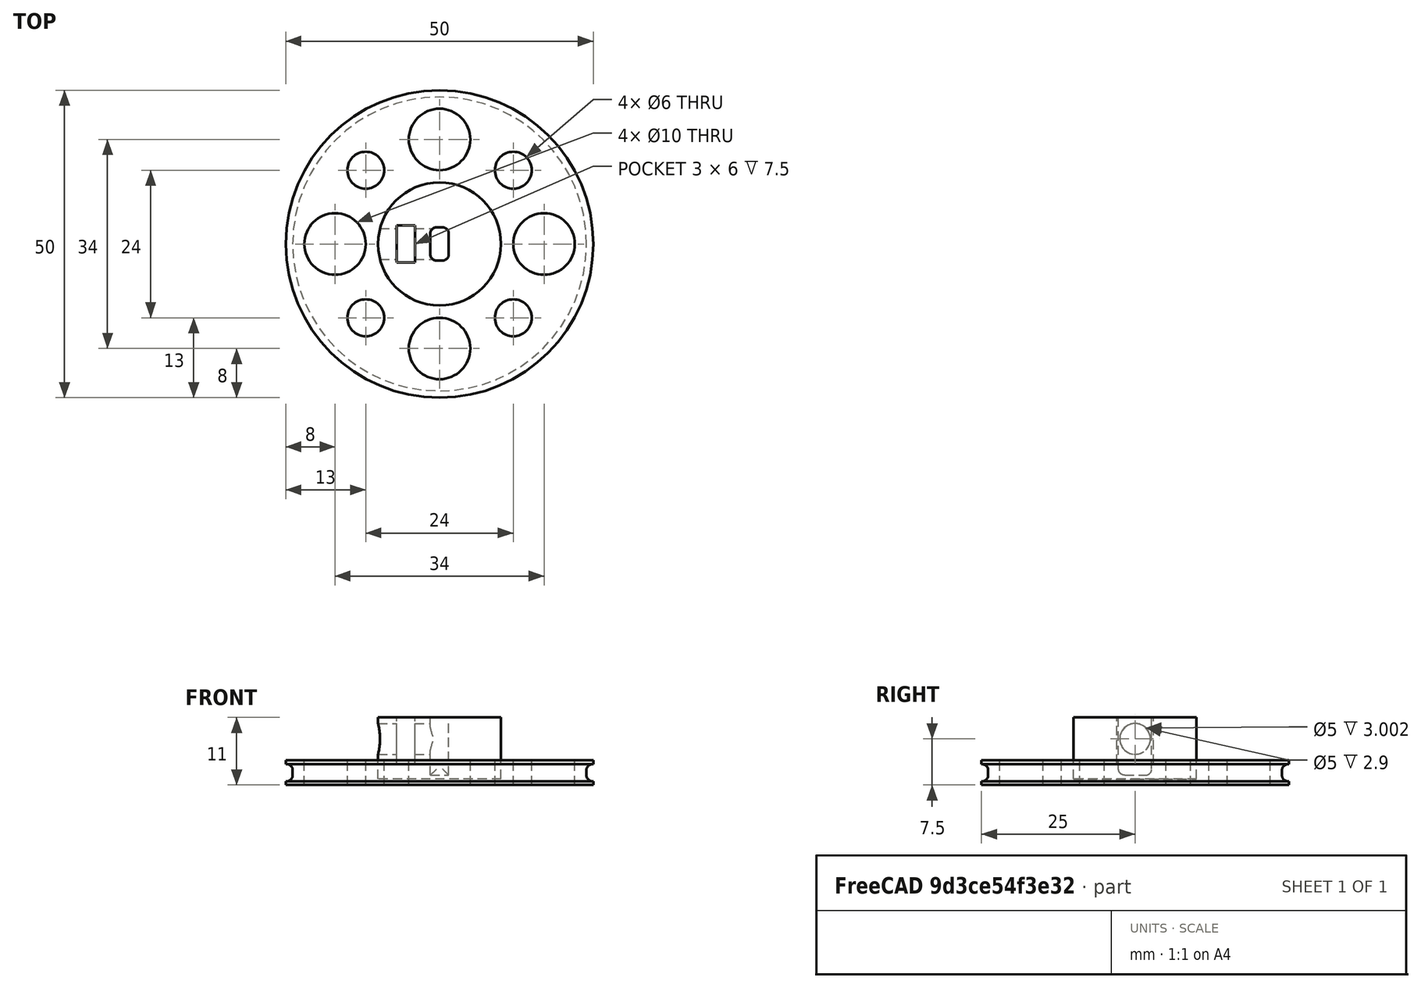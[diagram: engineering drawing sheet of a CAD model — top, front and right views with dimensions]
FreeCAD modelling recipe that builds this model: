
FCSTD DOCUMENT  (FreeCAD 0.18.4R)
Label: ruedas
License: All rights reserved
LicenseURL: http://en.wikipedia.org/wiki/All_rights_reserved
objects: Part::Cylinder×13, Part::Cut×13, Part::Fillet×2, Part::Box×2
note: 30 computed .brp shape members not serialized (recipe doc carries the construction recipe); baked Part::Feature solids carry a one-line shape summary decoded from their .brp

FEATURE [Part::Cylinder] Cylinder  label="Cilindro"
  Angle = 360
  AttacherType = Attacher::AttachEngine3D
  Height = 4
  Radius = 25
FEATURE [Part::Cylinder] Cylinder002  label="Cilindro002"
  Angle = 360
  AttacherType = Attacher::AttachEngine3D
  Height = 15
  Placement = pos=(17,0,-2) rot=(0,0,1;0rad)
  Radius = 5
FEATURE [Part::Cylinder] Cylinder003  label="Cilindro003"
  Angle = 360
  AttacherType = Attacher::AttachEngine3D
  Height = 15
  Placement = pos=(-17,0,-2) rot=(0,0,1;0rad)
  Radius = 5
FEATURE [Part::Cylinder] Cylinder004  label="Cilindro004"
  Angle = 360
  AttacherType = Attacher::AttachEngine3D
  Height = 15
  Placement = pos=(0,17,-2) rot=(0,0,1;0rad)
  Radius = 5
FEATURE [Part::Cylinder] Cylinder005  label="Cilindro005"
  Angle = 360
  AttacherType = Attacher::AttachEngine3D
  Height = 15
  Placement = pos=(0,-17,-2) rot=(0,0,1;0rad)
  Radius = 5
FEATURE [Part::Cylinder] Cylinder006  label="Cilindro006"
  Angle = 360
  AttacherType = Attacher::AttachEngine3D
  Height = 10
  Placement = pos=(-12,-12,-2) rot=(0,0,1;0rad)
  Radius = 3
FEATURE [Part::Cylinder] Cylinder007  label="Cilindro007"
  Angle = 360
  AttacherType = Attacher::AttachEngine3D
  Height = 10
  Placement = pos=(-12,12,-2) rot=(0,0,1;0rad)
  Radius = 3
FEATURE [Part::Cylinder] Cylinder008  label="Cilindro008"
  Angle = 360
  AttacherType = Attacher::AttachEngine3D
  Height = 10
  Placement = pos=(12,-12,-2) rot=(0,0,1;0rad)
  Radius = 3
FEATURE [Part::Cylinder] Cylinder009  label="Cilindro009"
  Angle = 360
  AttacherType = Attacher::AttachEngine3D
  Height = 10
  Placement = pos=(12,12,-2) rot=(0,0,1;0rad)
  Radius = 3
FEATURE [Part::Cut] Cut
  Base = -> Cylinder
  Tool = -> Cylinder004
FEATURE [Part::Cut] Cut001
  Base = -> Cut
  Tool = -> Cylinder007
FEATURE [Part::Cut] Cut002
  Base = -> Cut001
  Tool = -> Cylinder003
FEATURE [Part::Cut] Cut003
  Base = -> Cut002
  Tool = -> Cylinder006
FEATURE [Part::Cut] Cut004
  Base = -> Cut003
  Tool = -> Cylinder005
FEATURE [Part::Cut] Cut005
  Base = -> Cut004
  Tool = -> Cylinder008
FEATURE [Part::Cut] Cut006
  Base = -> Cut005
  Tool = -> Cylinder002
FEATURE [Part::Cut] Cut007
  Base = -> Cut006
  Tool = -> Cylinder009
FEATURE [Part::Cylinder] Cylinder010  label="Cilindro010"
  Angle = 360
  AttacherType = Attacher::AttachEngine3D
  Height = 2.8
  Placement = pos=(0,0,0.6) rot=(0,0,1;0rad)
  Radius = 25
FEATURE [Part::Cylinder] Cylinder011  label="Cilindro011"
  Angle = 360
  AttacherType = Attacher::AttachEngine3D
  Height = 2.8
  Placement = pos=(0,0,0.6) rot=(0,0,1;0rad)
  Radius = 23.9
FEATURE [Part::Cut] Cut008
  Base = -> Cylinder010
  Tool = -> Cylinder011
FEATURE [Part::Cut] Cut009
  Base = -> Cut007
  Tool = -> Cut008
FEATURE [Part::Fillet] Fillet
  Base = -> Cut009
  Edges = 2 edges r=1: [Edge4,Edge14]
FEATURE [Part::Cylinder] Cylinder012  label="Cilindro012"
  Angle = 360
  AttacherType = Attacher::AttachEngine3D
  Height = 10
  Radius = 10
FEATURE [Part::Box] Box  label="Cubo"
  AttacherType = Attacher::AttachEngine3D
  Height = 15
  Length = 3
  Placement = pos=(-1.5,-2.7,0.6) rot=(0,0,1;0rad)
  Width = 5.4
FEATURE [Part::Fillet] Fillet001
  Base = -> Box
  Edges = 8 edges r=1: [Edge1,Edge3,Edge5,Edge7,Edge9,Edge10,Edge11,Edge12]
FEATURE [Part::Cylinder] Cylinder013  label="Cilindro013"
  Angle = 360
  AttacherType = Attacher::AttachEngine3D
  Height = 15
  Placement = pos=(-15,0,6.5) rot=(0,1,0;1.5708rad)
  Radius = 2.5
FEATURE [Part::Box] Box001  label="Cubo001"
  AttacherType = Attacher::AttachEngine3D
  Height = 15
  Length = 3
  Placement = pos=(-7,-3,2.5) rot=(0,0,1;0rad)
  Width = 6
FEATURE [Part::Cut] Cut010
  Base = -> Cylinder012
  Tool = -> Box001
FEATURE [Part::Cut] Cut011
  Base = -> Cut010
  Tool = -> Fillet001
FEATURE [Part::Cut] Cut012
  Base = -> Cut011
  Placement = pos=(0,0,1) rot=(0,0,1;0rad)
  Tool = -> Cylinder013
